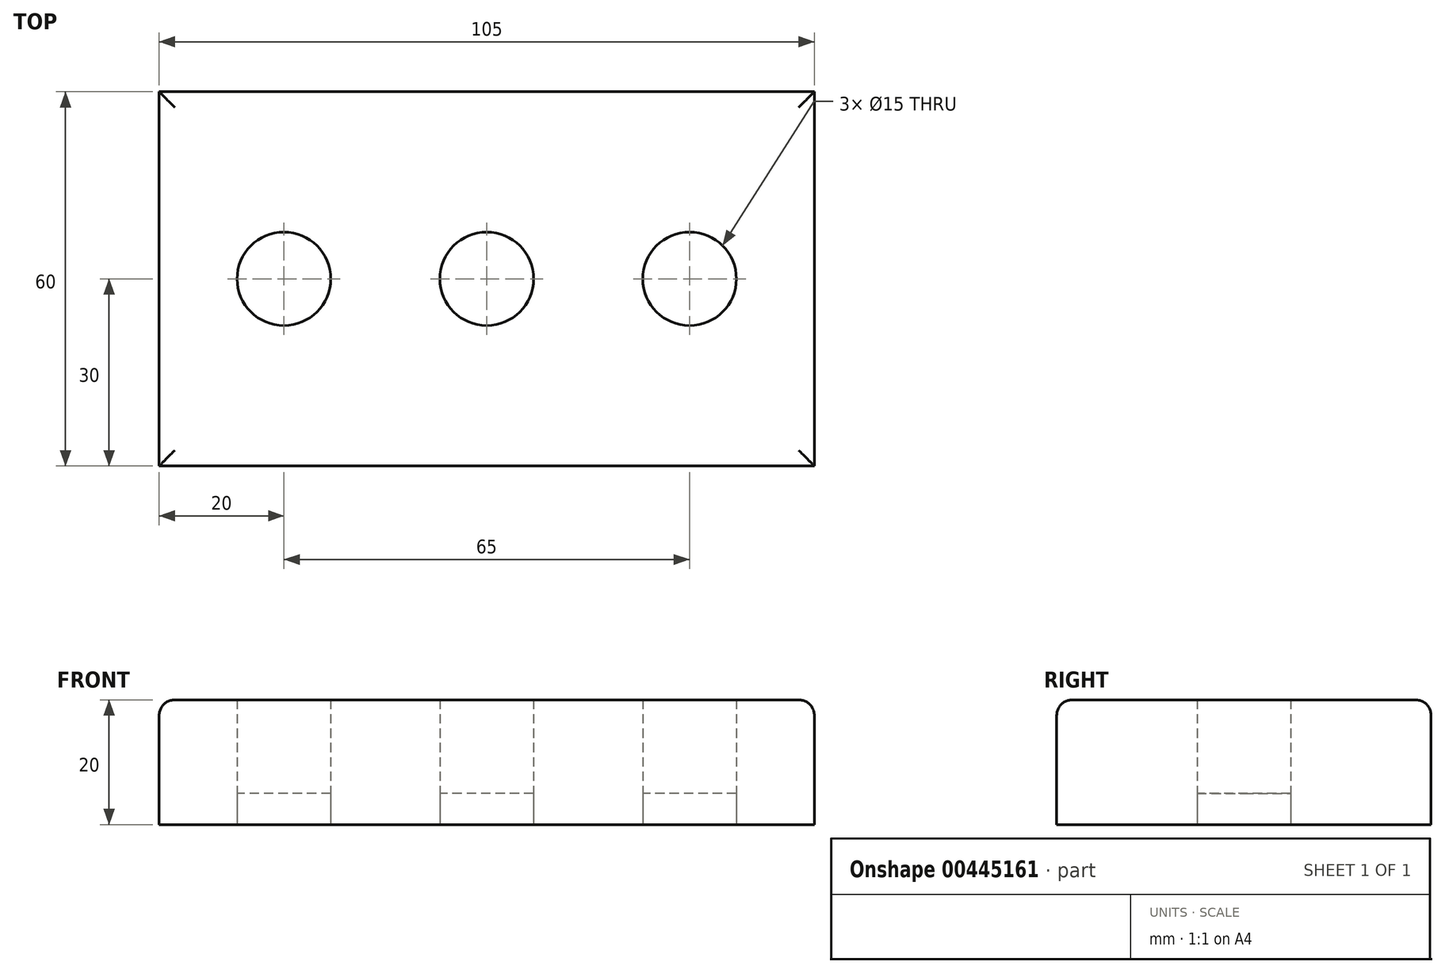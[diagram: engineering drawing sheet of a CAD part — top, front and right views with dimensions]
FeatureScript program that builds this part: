
annotation { "Feature Type Name" : "Feature", "Feature Type Description" : "" }
export const myFeature = defineFeature(function(context is Context, id is Id, definition is map)
    precondition{}
    {
        {
            var Q0;
            Q0=qCreatedBy(makeId("Top.planeOp"),FACE);
            var sketch = newSketch(context, id + "F0", { "sketchPlane" : qUnion([Q0])});
            skLineSegment(sketch, "E0.bottom", {"start": v(52.5, 30) * mm, "end": v(-52.5, 30) * mm});
            skLineSegment(sketch, "E0.top", {"start": v(52.5, -30) * mm, "end": v(-52.5, -30) * mm});
            skLineSegment(sketch, "E0.left", {"start": v(52.5, 30) * mm, "end": v(52.5, -30) * mm});
            skLineSegment(sketch, "E0.right", {"start": v(-52.5, 30) * mm, "end": v(-52.5, -30) * mm});
            skPoint(sketch, "E0.middle", {"position": v(0, 0) * mm});
            skCircle(sketch, "E1", {"center": v(0, 0) * mm, "radius": 7.5 * mm});
            skLineSegment(sketch, "E2", {"start": v(7.5, 0) * mm, "end": v(17.5, 0) * mm});
            skLineSegment(sketch, "E3", {"start": v(-7.5, 0) * mm, "end": v(-17.5, 0) * mm});
            skLineSegment(sketch, "E4", {"start": v(17.5, 0) * mm, "end": v(32.5, 0) * mm});
            skLineSegment(sketch, "E5", {"start": v(-17.5, 0) * mm, "end": v(-32.5, 0) * mm});
            skCircle(sketch, "E6", {"center": v(-32.5, 0) * mm, "radius": 7.5 * mm});
            skCircle(sketch, "E7", {"center": v(32.5, 0) * mm, "radius": 7.5 * mm});
            skSolve(sketch);
        }
        {
            var Q0;
            Q0 = qSketchRegion(id + "F0", true);
            extrude(context, id + "F1", {"entities" : qUnion([Q0]), "depth" : 20 * mm});
        }
        {
            var Q0;
            Q0=makeQuery(id+"F0.imprint","IMPRINT",FACE,{"disambiguationData":[TD([[makeQuery(id+"F0.imprint","IMPRINT",EDGE,{"derivedFrom":sQuery(id+"F0.wireOp",EDGE,"E6")}),1.0]])]});
            var Q1;
            Q1=makeQuery(id+"F0.imprint","IMPRINT",FACE,{"disambiguationData":[TD([[makeQuery(id+"F0.imprint","IMPRINT",EDGE,{"derivedFrom":sQuery(id+"F0.wireOp",EDGE,"E7")}),1.0]])]});
            var Q2;
            {var subQ0=sQuery(id+"F0.wireOp",EDGE,"E1");var subQ1=makeQuery(id+"F0.imprint","IMPRINT",VERTEX,{"disambiguationData":[OD(0.0)],"derivedFrom":subQ0});Q2=makeQuery(id+"F0.imprint","IMPRINT",FACE,{"disambiguationData":[TD([[makeQuery(id+"F0.imprint","IMPRINT",EDGE,{"disambiguationData":[TD([[subQ1,-1.0]])],"derivedFrom":subQ0}),1.0]])]});}
            extrude(context, id + "F2", {"entities" : qUnion([Q0, Q1, Q2]), "depth" : 5 * mm});
        }
        {
            var Q0;
            Q0=makeQuery(id+"F1.opExtrude","CAP_EDGE",EDGE,{"disambiguationData":[OSD([sQuery(id+"F0.wireOp",EDGE,"E0.top")])],"isStart":false});
            var Q1;
            Q1=makeQuery(id+"F1.opExtrude","CAP_EDGE",EDGE,{"disambiguationData":[OSD([sQuery(id+"F0.wireOp",EDGE,"E0.right")])],"isStart":false});
            var Q2;
            Q2=makeQuery(id+"F1.opExtrude","CAP_EDGE",EDGE,{"disambiguationData":[OSD([sQuery(id+"F0.wireOp",EDGE,"E0.bottom")])],"isStart":false});
            var Q3;
            Q3=makeQuery(id+"F1.opExtrude","CAP_EDGE",EDGE,{"disambiguationData":[OSD([sQuery(id+"F0.wireOp",EDGE,"E0.left")])],"isStart":false});
            fillet(context, id + "F3", {"entities" : qUnion([Q0, Q1, Q2, Q3]), "radius" : 2.5 * mm, "tangentPropagation" : true, "allowEdgeOverflow" : false});
        }
    });
